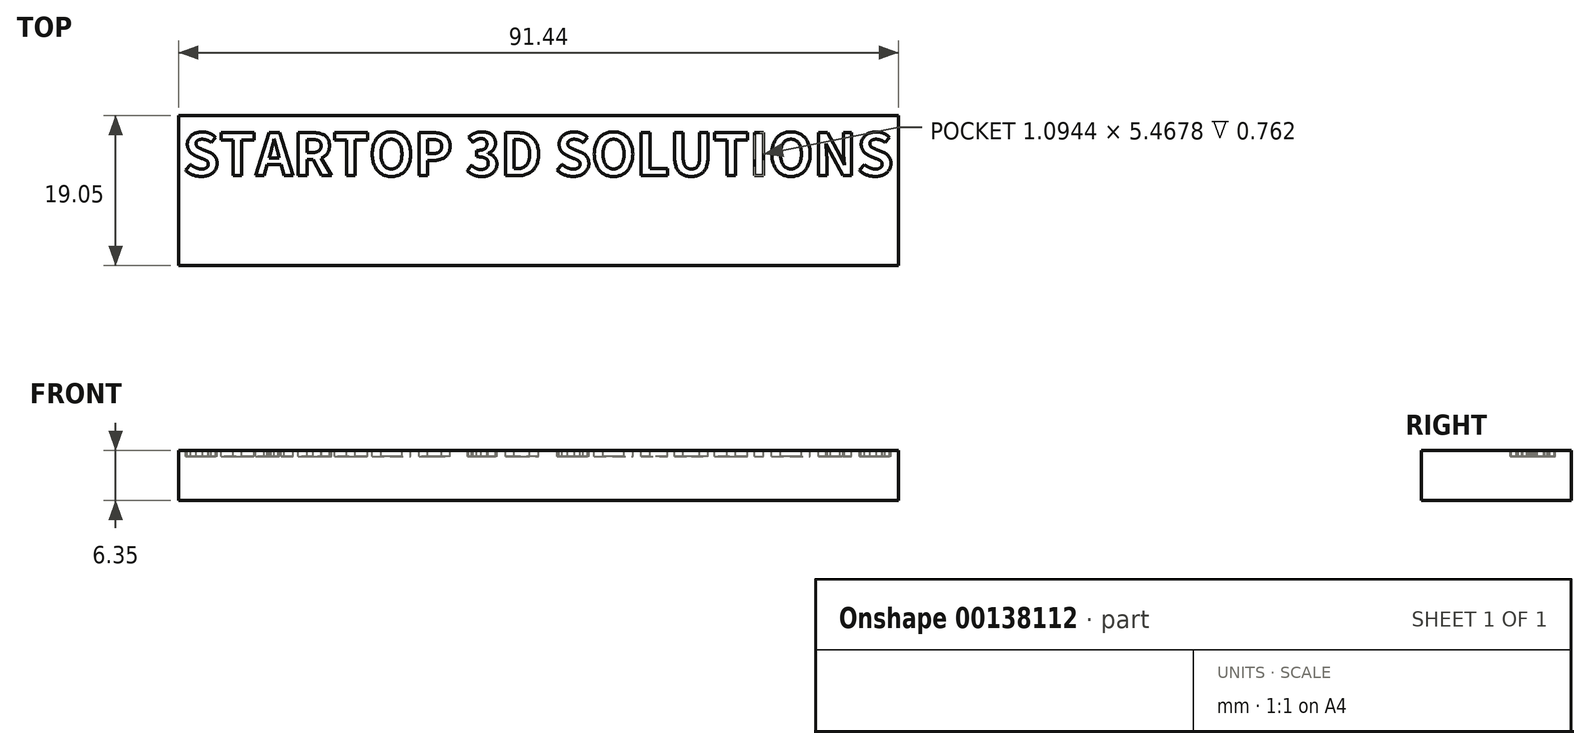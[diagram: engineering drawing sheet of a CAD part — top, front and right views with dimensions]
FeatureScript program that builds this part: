
annotation { "Feature Type Name" : "Feature", "Feature Type Description" : "" }
export const myFeature = defineFeature(function(context is Context, id is Id, definition is map)
    precondition{}
    {
        {
            var Q0;
            Q0=qCreatedBy(makeId("Top.planeOp"),FACE);
            var sketch = newSketch(context, id + "F0", { "sketchPlane" : qUnion([Q0])});
            skLineSegment(sketch, "E0.bottom", {"start": v(0, 0) * mm, "end": v(91.44, 0) * mm});
            skLineSegment(sketch, "E0.top", {"start": v(0, 19.05) * mm, "end": v(91.44, 19.05) * mm});
            skLineSegment(sketch, "E0.left", {"start": v(0, 0) * mm, "end": v(0, 19.05) * mm});
            skLineSegment(sketch, "E0.right", {"start": v(91.44, 0) * mm, "end": v(91.44, 19.05) * mm});
            skSolve(sketch);
        }
        {
            var Q0;
            Q0=qSketchRegion(id+"F0",true);
            extrude(context, id + "F1", {"entities" : qUnion([Q0]), "depth" : 6.35 * mm});
        }
        {
            var Q0;
            Q0=makeQuery(id+"F1.opExtrude","CAP_FACE",FACE,{"disambiguationData":[OSD([sQuery(id+"F0.wireOp",EDGE,"E0.bottom"),sQuery(id+"F0.wireOp",EDGE,"E0.top"),sQuery(id+"F0.wireOp",EDGE,"E0.left"),sQuery(id+"F0.wireOp",EDGE,"E0.right")])],"isStart":false});
            var sketch = newSketch(context, id + "F2", { "sketchPlane" : qUnion([Q0])});
            skLineSegment(sketch, "E1", {"start": v(0, 9.53) * mm, "end": v(91.44, 9.53) * mm, "construction": true});
            skText(sketch, "E2", { "text": "STARTOP 3D SOLUTIONS", "fontName": "NotoSansCJKsc-Bold.otf"});
            const initialGuessF2  = {"E2": [0.00056, 0.0114, 1, 0, 0.00532]};
            skSetInitialGuess(sketch, initialGuessF2);
            skSolve(sketch);
        }
        {
            var Q0;
            Q0=qSketchRegion(id+"F2",true);
            extrude(context, id + "F3", {"entities" : qUnion([Q0]), "operationType" : NewBodyOperationType.REMOVE, "oppositeDirection" : true, "depth" : 0.76 * mm});
        }
    });
